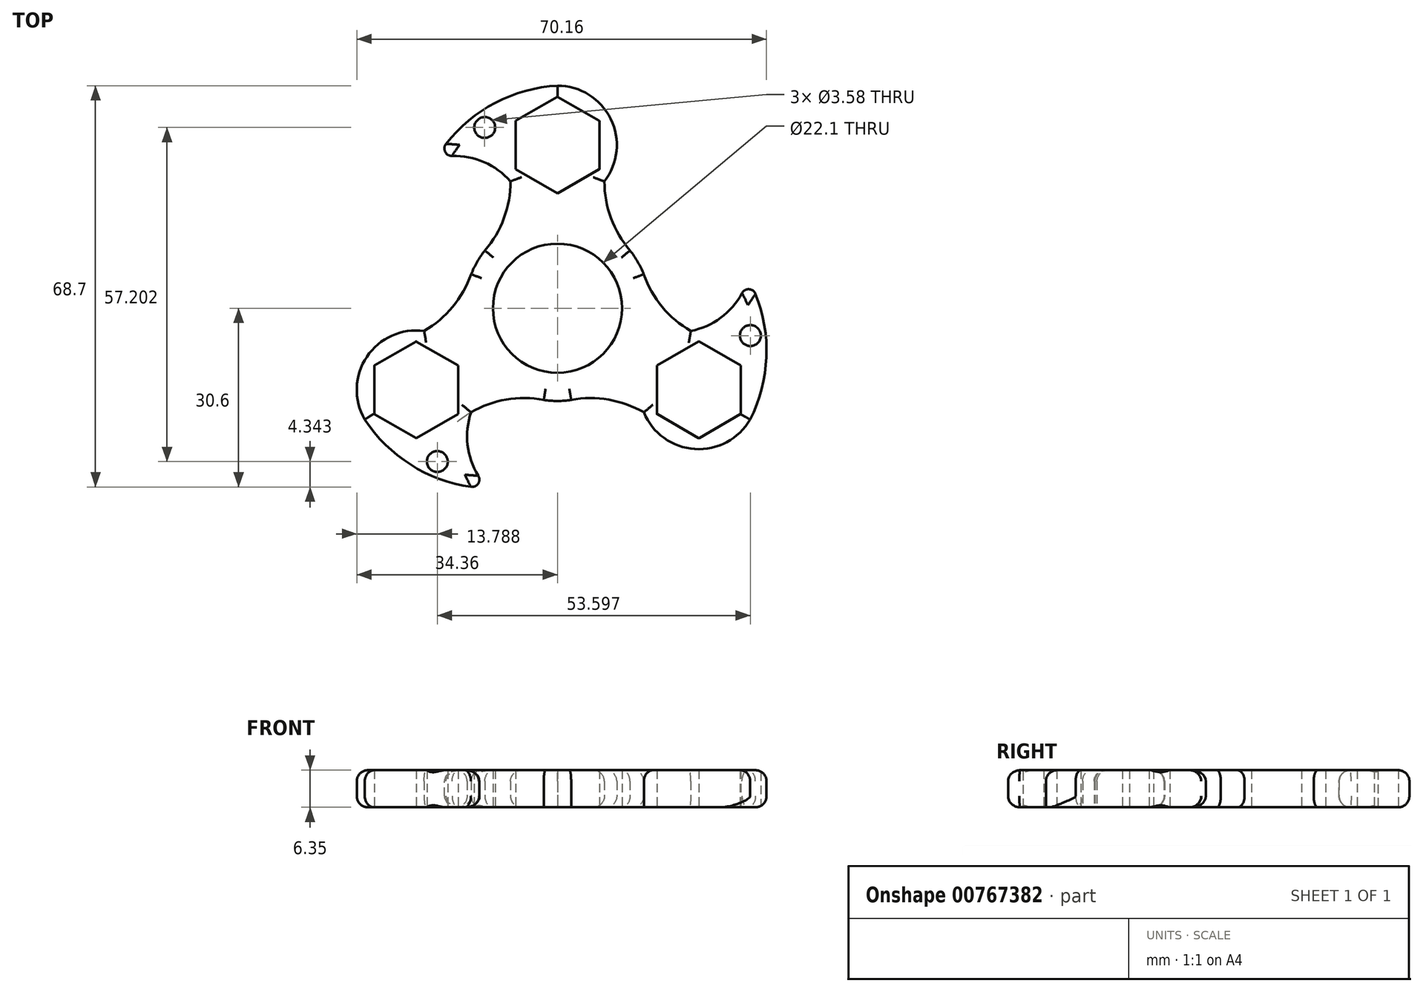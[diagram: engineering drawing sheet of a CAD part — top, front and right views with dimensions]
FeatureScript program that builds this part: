
annotation { "Feature Type Name" : "Feature", "Feature Type Description" : "" }
export const myFeature = defineFeature(function(context is Context, id is Id, definition is map)
    precondition{}
    {
        {
            var Q0;
            Q0=qCreatedBy(makeId("Top.planeOp"),FACE);
            var sketch = newSketch(context, id + "F0", { "sketchPlane" : qUnion([Q0])});
            skCircle(sketch, "E0", {"center": v(0, 0) * mm, "radius": 38.1 * mm});
            skCircle(sketch, "E1", {"center": v(0, 0) * mm, "radius": 11.05 * mm});
            skCircle(sketch, "E2.cCircle", {"center": v(0, 27.94) * mm, "radius": 8.29 * mm, "construction": true});
            skLineSegment(sketch, "E2.0", {"start": v(0, 36.23) * mm, "end": v(7.18, 32.08) * mm});
            skLineSegment(sketch, "E2.1", {"start": v(7.18, 32.08) * mm, "end": v(7.18, 23.8) * mm});
            skLineSegment(sketch, "E2.2", {"start": v(7.18, 23.8) * mm, "end": v(0, 19.65) * mm});
            skLineSegment(sketch, "E2.3", {"start": v(0, 19.65) * mm, "end": v(-7.18, 23.8) * mm});
            skLineSegment(sketch, "E2.4", {"start": v(-7.18, 23.8) * mm, "end": v(-7.18, 32.08) * mm});
            skLineSegment(sketch, "E2.5", {"start": v(-7.18, 32.08) * mm, "end": v(0, 36.23) * mm});
            skCircle(sketch, "E3", {"center": v(0, 27.94) * mm, "radius": 10.16 * mm});
            skCircle(sketch, "E4", {"center": v(0, 0) * mm, "radius": 15.88 * mm});
            skArc(sketch, "E5", {"start": v(8.04, 21.73) * mm, "mid": v(9.17, 15.41) * mm, "end": v(12.42, 9.88) * mm});
            skPoint(sketch, "E5.startSnap0", {"position": v(-3.59, 21.73) * mm});
            skArc(sketch, "E6", {"start": v(-12.42, 9.88) * mm, "mid": v(-9.16, 15.4) * mm, "end": v(-8.04, 21.73) * mm});
            skArc(sketch, "E7", {"start": v(0, 38.1) * mm, "mid": v(-11.9, 34.46) * mm, "end": v(-20.76, 25.7) * mm});
            skArc(sketch, "E8", {"start": v(-8.04, 21.73) * mm, "mid": v(-13.84, 25.5) * mm, "end": v(-20.76, 25.7) * mm});
            skCircle(sketch, "E9", {"center": v(-12.45, 30.94) * mm, "radius": 1.79 * mm});
            skArc(sketch, "E10.1.0", {"start": v(-14.8, -17.82) * mm, "mid": v(-15.16, -24.73) * mm, "end": v(-11.88, -30.83) * mm});
            skArc(sketch, "E10.1.1", {"start": v(-2.35, -15.7) * mm, "mid": v(-8.76, -15.64) * mm, "end": v(-14.8, -17.82) * mm});
            skArc(sketch, "E10.1.2", {"start": v(-33, -19.05) * mm, "mid": v(-23.89, -27.54) * mm, "end": v(-11.88, -30.83) * mm});
            skCircle(sketch, "E10.1.3", {"center": v(-24.2, -13.97) * mm, "radius": 10.16 * mm});
            skArc(sketch, "E10.1.4", {"start": v(-22.83, -3.9) * mm, "mid": v(-17.94, 0.24) * mm, "end": v(-14.77, 5.82) * mm});
            skCircle(sketch, "E10.1.5", {"center": v(-20.57, -26.26) * mm, "radius": 1.79 * mm});
            skLineSegment(sketch, "E10.1.6", {"start": v(-17.02, -18.11) * mm, "end": v(-24.2, -22.26) * mm});
            skLineSegment(sketch, "E10.1.7", {"start": v(-24.2, -22.26) * mm, "end": v(-31.37, -18.11) * mm});
            skLineSegment(sketch, "E10.1.8", {"start": v(-31.37, -18.11) * mm, "end": v(-31.37, -9.83) * mm});
            skLineSegment(sketch, "E10.1.9", {"start": v(-31.37, -9.83) * mm, "end": v(-24.2, -5.68) * mm});
            skLineSegment(sketch, "E10.1.10", {"start": v(-24.2, -5.68) * mm, "end": v(-17.02, -9.83) * mm});
            skLineSegment(sketch, "E10.1.11", {"start": v(-17.02, -9.83) * mm, "end": v(-17.02, -18.11) * mm});
            skArc(sketch, "E10.2.0", {"start": v(22.83, -3.9) * mm, "mid": v(29, -0.76) * mm, "end": v(32.64, 5.13) * mm});
            skArc(sketch, "E10.2.1", {"start": v(14.77, 5.82) * mm, "mid": v(17.93, 0.23) * mm, "end": v(22.83, -3.9) * mm});
            skArc(sketch, "E10.2.2", {"start": v(33, -19.05) * mm, "mid": v(35.8, -6.92) * mm, "end": v(32.64, 5.13) * mm});
            skCircle(sketch, "E10.2.3", {"center": v(24.2, -13.97) * mm, "radius": 10.16 * mm});
            skArc(sketch, "E10.2.4", {"start": v(14.8, -17.82) * mm, "mid": v(8.76, -15.65) * mm, "end": v(2.35, -15.7) * mm});
            skCircle(sketch, "E10.2.5", {"center": v(33.03, -4.69) * mm, "radius": 1.79 * mm});
            skLineSegment(sketch, "E10.2.6", {"start": v(24.2, -5.68) * mm, "end": v(31.37, -9.83) * mm});
            skLineSegment(sketch, "E10.2.7", {"start": v(31.37, -9.83) * mm, "end": v(31.37, -18.11) * mm});
            skLineSegment(sketch, "E10.2.8", {"start": v(31.37, -18.11) * mm, "end": v(24.2, -22.26) * mm});
            skLineSegment(sketch, "E10.2.9", {"start": v(24.2, -22.26) * mm, "end": v(17.02, -18.11) * mm});
            skLineSegment(sketch, "E10.2.10", {"start": v(17.02, -18.11) * mm, "end": v(17.02, -9.83) * mm});
            skLineSegment(sketch, "E10.2.11", {"start": v(17.02, -9.83) * mm, "end": v(24.2, -5.68) * mm});
            skSolve(sketch);
        }
        {
            var Q0;
            {var subQ0=sQuery(id+"F0.wireOp",EDGE,"E5");Q0=makeQuery(id+"F0.imprint","IMPRINT",FACE,{"disambiguationData":[TD([[makeQuery(id+"F0.imprint","IMPRINT",EDGE,{"derivedFrom":subQ0}),-1.0]])]});}
            var Q1;
            Q1=makeQuery(id+"F0.imprint","IMPRINT",FACE,{"disambiguationData":[TD([[makeQuery(id+"F0.imprint","IMPRINT",EDGE,{"derivedFrom":sQuery(id+"F0.wireOp",EDGE,"E2.0")}),1.0]])]});
            var Q2;
            {var subQ0=sQuery(id+"F0.wireOp",EDGE,"E8");Q2=makeQuery(id+"F0.imprint","IMPRINT",FACE,{"disambiguationData":[TD([[makeQuery(id+"F0.imprint","IMPRINT",EDGE,{"derivedFrom":subQ0}),-1.0]])]});}
            var Q3;
            Q3=makeQuery(id+"F0.imprint","IMPRINT",FACE,{"disambiguationData":[TD([[makeQuery(id+"F0.imprint","IMPRINT",EDGE,{"derivedFrom":sQuery(id+"F0.wireOp",EDGE,"E1")}),-1.0]])]});
            var Q4;
            Q4=makeQuery(id+"F0.imprint","IMPRINT",FACE,{"disambiguationData":[TD([[makeQuery(id+"F0.imprint","IMPRINT",EDGE,{"derivedFrom":sQuery(id+"F0.wireOp",EDGE,"E10.1.6")}),1.0]])]});
            var Q5;
            {var subQ0=sQuery(id+"F0.wireOp",EDGE,"E10.1.1");Q5=makeQuery(id+"F0.imprint","IMPRINT",FACE,{"disambiguationData":[TD([[makeQuery(id+"F0.imprint","IMPRINT",EDGE,{"derivedFrom":subQ0}),-1.0]])]});}
            var Q6;
            {var subQ1=sQuery(id+"F0.wireOp",EDGE,"E10.1.0");Q6=makeQuery(id+"F0.imprint","IMPRINT",FACE,{"disambiguationData":[TD([[makeQuery(id+"F0.imprint","IMPRINT",EDGE,{"derivedFrom":subQ1}),-1.0]])]});}
            var Q7;
            {var subQ0=sQuery(id+"F0.wireOp",EDGE,"E10.2.1");Q7=makeQuery(id+"F0.imprint","IMPRINT",FACE,{"disambiguationData":[TD([[makeQuery(id+"F0.imprint","IMPRINT",EDGE,{"derivedFrom":subQ0}),-1.0]])]});}
            var Q8;
            Q8=makeQuery(id+"F0.imprint","IMPRINT",FACE,{"disambiguationData":[TD([[makeQuery(id+"F0.imprint","IMPRINT",EDGE,{"derivedFrom":sQuery(id+"F0.wireOp",EDGE,"E10.2.6")}),1.0]])]});
            var Q9;
            {var subQ1=sQuery(id+"F0.wireOp",EDGE,"E10.2.0");Q9=makeQuery(id+"F0.imprint","IMPRINT",FACE,{"disambiguationData":[TD([[makeQuery(id+"F0.imprint","IMPRINT",EDGE,{"derivedFrom":subQ1}),-1.0]])]});}
            extrude(context, id + "F1", {"entities" : qUnion([Q0, Q1, Q2, Q3, Q4, Q5, Q6, Q7, Q8, Q9]), "depth" : 6.35 * mm, "offsetDistance" : 25.4 * mm});
        }
        {
            var Q0;
            Q0=makeQuery(id+"F1.opExtrude","SWEPT_EDGE",EDGE,{"disambiguationData":[OSD([sQuery(id+"F0.wireOp",EDGE,"E7"),sQuery(id+"F0.wireOp",EDGE,"E8")])]});
            var Q1;
            Q1=makeQuery(id+"F1.opExtrude","SWEPT_EDGE",EDGE,{"disambiguationData":[OSD([sQuery(id+"F0.wireOp",EDGE,"E10.1.0"),sQuery(id+"F0.wireOp",EDGE,"E10.1.2")])]});
            var Q2;
            Q2=makeQuery(id+"F1.opExtrude","SWEPT_EDGE",EDGE,{"disambiguationData":[OSD([sQuery(id+"F0.wireOp",EDGE,"E10.2.0"),sQuery(id+"F0.wireOp",EDGE,"E10.2.2")])]});
            fillet(context, id + "F2", {"entities" : qUnion([Q0, Q1, Q2]), "radius" : 1.27 * mm, "tangentPropagation" : true, "allowEdgeOverflow" : false});
        }
        {
            var Q0;
            {var subQ0=sQuery(id+"F0.wireOp",EDGE,"E10.1.2");var subQ1=sQuery(id+"F0.wireOp",EDGE,"E10.1.0");Q0=makeQuery(id+"F2.opFillet","BLEND_EDGE",EDGE,{"blendedFrom":[makeQuery(id+"F1.opExtrude","SWEPT_EDGE",EDGE,{"disambiguationData":[OSD([subQ1,subQ0])]}),makeQuery(id+"F1.opExtrude","CAP_FACE",FACE,{"disambiguationData":[OSD([sQuery(id+"F0.wireOp",EDGE,"E1"),sQuery(id+"F0.wireOp",EDGE,"E2.0"),sQuery(id+"F0.wireOp",EDGE,"E2.1"),sQuery(id+"F0.wireOp",EDGE,"E2.2"),sQuery(id+"F0.wireOp",EDGE,"E2.3"),sQuery(id+"F0.wireOp",EDGE,"E2.4"),sQuery(id+"F0.wireOp",EDGE,"E2.5"),sQuery(id+"F0.wireOp",EDGE,"E3"),sQuery(id+"F0.wireOp",EDGE,"E4"),sQuery(id+"F0.wireOp",EDGE,"E5"),sQuery(id+"F0.wireOp",EDGE,"E6"),sQuery(id+"F0.wireOp",EDGE,"E7"),sQuery(id+"F0.wireOp",EDGE,"E8"),sQuery(id+"F0.wireOp",EDGE,"E9"),subQ1,sQuery(id+"F0.wireOp",EDGE,"E10.1.1"),subQ0,sQuery(id+"F0.wireOp",EDGE,"E10.1.3"),sQuery(id+"F0.wireOp",EDGE,"E10.1.4"),sQuery(id+"F0.wireOp",EDGE,"E10.1.5"),sQuery(id+"F0.wireOp",EDGE,"E10.1.6"),sQuery(id+"F0.wireOp",EDGE,"E10.1.7"),sQuery(id+"F0.wireOp",EDGE,"E10.1.8"),sQuery(id+"F0.wireOp",EDGE,"E10.1.9"),sQuery(id+"F0.wireOp",EDGE,"E10.1.10"),sQuery(id+"F0.wireOp",EDGE,"E10.1.11"),sQuery(id+"F0.wireOp",EDGE,"E10.2.0"),sQuery(id+"F0.wireOp",EDGE,"E10.2.1"),sQuery(id+"F0.wireOp",EDGE,"E10.2.2"),sQuery(id+"F0.wireOp",EDGE,"E10.2.3"),sQuery(id+"F0.wireOp",EDGE,"E10.2.4"),sQuery(id+"F0.wireOp",EDGE,"E10.2.5"),sQuery(id+"F0.wireOp",EDGE,"E10.2.6"),sQuery(id+"F0.wireOp",EDGE,"E10.2.7"),sQuery(id+"F0.wireOp",EDGE,"E10.2.8"),sQuery(id+"F0.wireOp",EDGE,"E10.2.9"),sQuery(id+"F0.wireOp",EDGE,"E10.2.10"),sQuery(id+"F0.wireOp",EDGE,"E10.2.11")])],"isStart":false})],"blendedInto":[makeQuery(id+"F1.opExtrude","CAP_FACE",FACE,{"disambiguationData":[OSD([sQuery(id+"F0.wireOp",EDGE,"E1"),sQuery(id+"F0.wireOp",EDGE,"E2.0"),sQuery(id+"F0.wireOp",EDGE,"E2.1"),sQuery(id+"F0.wireOp",EDGE,"E2.2"),sQuery(id+"F0.wireOp",EDGE,"E2.3"),sQuery(id+"F0.wireOp",EDGE,"E2.4"),sQuery(id+"F0.wireOp",EDGE,"E2.5"),sQuery(id+"F0.wireOp",EDGE,"E3"),sQuery(id+"F0.wireOp",EDGE,"E4"),sQuery(id+"F0.wireOp",EDGE,"E5"),sQuery(id+"F0.wireOp",EDGE,"E6"),sQuery(id+"F0.wireOp",EDGE,"E7"),sQuery(id+"F0.wireOp",EDGE,"E8"),sQuery(id+"F0.wireOp",EDGE,"E9"),subQ1,sQuery(id+"F0.wireOp",EDGE,"E10.1.1"),subQ0,sQuery(id+"F0.wireOp",EDGE,"E10.1.3"),sQuery(id+"F0.wireOp",EDGE,"E10.1.4"),sQuery(id+"F0.wireOp",EDGE,"E10.1.5"),sQuery(id+"F0.wireOp",EDGE,"E10.1.6"),sQuery(id+"F0.wireOp",EDGE,"E10.1.7"),sQuery(id+"F0.wireOp",EDGE,"E10.1.8"),sQuery(id+"F0.wireOp",EDGE,"E10.1.9"),sQuery(id+"F0.wireOp",EDGE,"E10.1.10"),sQuery(id+"F0.wireOp",EDGE,"E10.1.11"),sQuery(id+"F0.wireOp",EDGE,"E10.2.0"),sQuery(id+"F0.wireOp",EDGE,"E10.2.1"),sQuery(id+"F0.wireOp",EDGE,"E10.2.2"),sQuery(id+"F0.wireOp",EDGE,"E10.2.3"),sQuery(id+"F0.wireOp",EDGE,"E10.2.4"),sQuery(id+"F0.wireOp",EDGE,"E10.2.5"),sQuery(id+"F0.wireOp",EDGE,"E10.2.6"),sQuery(id+"F0.wireOp",EDGE,"E10.2.7"),sQuery(id+"F0.wireOp",EDGE,"E10.2.8"),sQuery(id+"F0.wireOp",EDGE,"E10.2.9"),sQuery(id+"F0.wireOp",EDGE,"E10.2.10"),sQuery(id+"F0.wireOp",EDGE,"E10.2.11")])],"isStart":false})]});}
            var Q1;
            Q1=makeQuery(id+"F1.opExtrude","CAP_EDGE",EDGE,{"disambiguationData":[OSD([sQuery(id+"F0.wireOp",EDGE,"E10.1.1")])],"isStart":false});
            var Q2;
            Q2=makeQuery(id+"F1.opExtrude","CAP_EDGE",EDGE,{"disambiguationData":[OSD([sQuery(id+"F0.wireOp",EDGE,"E10.1.0")])],"isStart":false});
            var Q3;
            Q3=makeQuery(id+"F1.opExtrude","CAP_EDGE",EDGE,{"disambiguationData":[OSD([sQuery(id+"F0.wireOp",EDGE,"E10.2.4")])],"isStart":false});
            var Q4;
            Q4=makeQuery(id+"F1.opExtrude","CAP_EDGE",EDGE,{"disambiguationData":[OSD([sQuery(id+"F0.wireOp",EDGE,"E10.2.3")])],"isStart":false});
            var Q5;
            Q5=makeQuery(id+"F1.opExtrude","CAP_EDGE",EDGE,{"disambiguationData":[OSD([sQuery(id+"F0.wireOp",EDGE,"E10.2.2")])],"isStart":false});
            var Q6;
            Q6=makeQuery(id+"F1.opExtrude","CAP_EDGE",EDGE,{"disambiguationData":[OSD([sQuery(id+"F0.wireOp",EDGE,"E10.2.1")])],"isStart":false});
            var Q7;
            Q7=makeQuery(id+"F1.opExtrude","CAP_EDGE",EDGE,{"disambiguationData":[OSD([sQuery(id+"F0.wireOp",EDGE,"E5")])],"isStart":false});
            var Q8;
            Q8=makeQuery(id+"F1.opExtrude","CAP_EDGE",EDGE,{"disambiguationData":[OSD([sQuery(id+"F0.wireOp",EDGE,"E3")])],"isStart":false});
            var Q9;
            Q9=makeQuery(id+"F1.opExtrude","CAP_EDGE",EDGE,{"disambiguationData":[OSD([sQuery(id+"F0.wireOp",EDGE,"E7")])],"isStart":false});
            var Q10;
            Q10=makeQuery(id+"F1.opExtrude","CAP_EDGE",EDGE,{"disambiguationData":[OSD([sQuery(id+"F0.wireOp",EDGE,"E6")])],"isStart":false});
            var Q11;
            Q11=makeQuery(id+"F1.opExtrude","CAP_EDGE",EDGE,{"disambiguationData":[OSD([sQuery(id+"F0.wireOp",EDGE,"E10.1.4")])],"isStart":false});
            var Q12;
            Q12=makeQuery(id+"F1.opExtrude","CAP_EDGE",EDGE,{"disambiguationData":[OSD([sQuery(id+"F0.wireOp",EDGE,"E10.1.3")])],"isStart":false});
            var Q13;
            Q13=makeQuery(id+"F1.opExtrude","CAP_EDGE",EDGE,{"disambiguationData":[OSD([sQuery(id+"F0.wireOp",EDGE,"E10.1.4")])],"isStart":true});
            var Q14;
            Q14=makeQuery(id+"F1.opExtrude","CAP_EDGE",EDGE,{"disambiguationData":[OSD([sQuery(id+"F0.wireOp",EDGE,"E6")])],"isStart":true});
            var Q15;
            Q15=makeQuery(id+"F1.opExtrude","CAP_EDGE",EDGE,{"disambiguationData":[OSD([sQuery(id+"F0.wireOp",EDGE,"E10.1.3")])],"isStart":true});
            var Q16;
            Q16=makeQuery(id+"F1.opExtrude","CAP_EDGE",EDGE,{"disambiguationData":[OSD([sQuery(id+"F0.wireOp",EDGE,"E10.1.2")])],"isStart":true});
            var Q17;
            Q17=makeQuery(id+"F1.opExtrude","CAP_EDGE",EDGE,{"disambiguationData":[OSD([sQuery(id+"F0.wireOp",EDGE,"E7")])],"isStart":true});
            var Q18;
            {var subQ0=sQuery(id+"F0.wireOp",EDGE,"E8");var subQ1=sQuery(id+"F0.wireOp",EDGE,"E7");Q18=makeQuery(id+"F2.opFillet","BLEND_EDGE",EDGE,{"blendedFrom":[makeQuery(id+"F1.opExtrude","SWEPT_EDGE",EDGE,{"disambiguationData":[OSD([subQ1,subQ0])]}),makeQuery(id+"F1.opExtrude","CAP_FACE",FACE,{"disambiguationData":[OSD([sQuery(id+"F0.wireOp",EDGE,"E1"),sQuery(id+"F0.wireOp",EDGE,"E2.0"),sQuery(id+"F0.wireOp",EDGE,"E2.1"),sQuery(id+"F0.wireOp",EDGE,"E2.2"),sQuery(id+"F0.wireOp",EDGE,"E2.3"),sQuery(id+"F0.wireOp",EDGE,"E2.4"),sQuery(id+"F0.wireOp",EDGE,"E2.5"),sQuery(id+"F0.wireOp",EDGE,"E3"),sQuery(id+"F0.wireOp",EDGE,"E4"),sQuery(id+"F0.wireOp",EDGE,"E5"),sQuery(id+"F0.wireOp",EDGE,"E6"),subQ1,subQ0,sQuery(id+"F0.wireOp",EDGE,"E9"),sQuery(id+"F0.wireOp",EDGE,"E10.1.0"),sQuery(id+"F0.wireOp",EDGE,"E10.1.1"),sQuery(id+"F0.wireOp",EDGE,"E10.1.2"),sQuery(id+"F0.wireOp",EDGE,"E10.1.3"),sQuery(id+"F0.wireOp",EDGE,"E10.1.4"),sQuery(id+"F0.wireOp",EDGE,"E10.1.5"),sQuery(id+"F0.wireOp",EDGE,"E10.1.6"),sQuery(id+"F0.wireOp",EDGE,"E10.1.7"),sQuery(id+"F0.wireOp",EDGE,"E10.1.8"),sQuery(id+"F0.wireOp",EDGE,"E10.1.9"),sQuery(id+"F0.wireOp",EDGE,"E10.1.10"),sQuery(id+"F0.wireOp",EDGE,"E10.1.11"),sQuery(id+"F0.wireOp",EDGE,"E10.2.0"),sQuery(id+"F0.wireOp",EDGE,"E10.2.1"),sQuery(id+"F0.wireOp",EDGE,"E10.2.2"),sQuery(id+"F0.wireOp",EDGE,"E10.2.3"),sQuery(id+"F0.wireOp",EDGE,"E10.2.4"),sQuery(id+"F0.wireOp",EDGE,"E10.2.5"),sQuery(id+"F0.wireOp",EDGE,"E10.2.6"),sQuery(id+"F0.wireOp",EDGE,"E10.2.7"),sQuery(id+"F0.wireOp",EDGE,"E10.2.8"),sQuery(id+"F0.wireOp",EDGE,"E10.2.9"),sQuery(id+"F0.wireOp",EDGE,"E10.2.10"),sQuery(id+"F0.wireOp",EDGE,"E10.2.11")])],"isStart":true})],"blendedInto":[makeQuery(id+"F1.opExtrude","CAP_FACE",FACE,{"disambiguationData":[OSD([sQuery(id+"F0.wireOp",EDGE,"E1"),sQuery(id+"F0.wireOp",EDGE,"E2.0"),sQuery(id+"F0.wireOp",EDGE,"E2.1"),sQuery(id+"F0.wireOp",EDGE,"E2.2"),sQuery(id+"F0.wireOp",EDGE,"E2.3"),sQuery(id+"F0.wireOp",EDGE,"E2.4"),sQuery(id+"F0.wireOp",EDGE,"E2.5"),sQuery(id+"F0.wireOp",EDGE,"E3"),sQuery(id+"F0.wireOp",EDGE,"E4"),sQuery(id+"F0.wireOp",EDGE,"E5"),sQuery(id+"F0.wireOp",EDGE,"E6"),subQ1,subQ0,sQuery(id+"F0.wireOp",EDGE,"E9"),sQuery(id+"F0.wireOp",EDGE,"E10.1.0"),sQuery(id+"F0.wireOp",EDGE,"E10.1.1"),sQuery(id+"F0.wireOp",EDGE,"E10.1.2"),sQuery(id+"F0.wireOp",EDGE,"E10.1.3"),sQuery(id+"F0.wireOp",EDGE,"E10.1.4"),sQuery(id+"F0.wireOp",EDGE,"E10.1.5"),sQuery(id+"F0.wireOp",EDGE,"E10.1.6"),sQuery(id+"F0.wireOp",EDGE,"E10.1.7"),sQuery(id+"F0.wireOp",EDGE,"E10.1.8"),sQuery(id+"F0.wireOp",EDGE,"E10.1.9"),sQuery(id+"F0.wireOp",EDGE,"E10.1.10"),sQuery(id+"F0.wireOp",EDGE,"E10.1.11"),sQuery(id+"F0.wireOp",EDGE,"E10.2.0"),sQuery(id+"F0.wireOp",EDGE,"E10.2.1"),sQuery(id+"F0.wireOp",EDGE,"E10.2.2"),sQuery(id+"F0.wireOp",EDGE,"E10.2.3"),sQuery(id+"F0.wireOp",EDGE,"E10.2.4"),sQuery(id+"F0.wireOp",EDGE,"E10.2.5"),sQuery(id+"F0.wireOp",EDGE,"E10.2.6"),sQuery(id+"F0.wireOp",EDGE,"E10.2.7"),sQuery(id+"F0.wireOp",EDGE,"E10.2.8"),sQuery(id+"F0.wireOp",EDGE,"E10.2.9"),sQuery(id+"F0.wireOp",EDGE,"E10.2.10"),sQuery(id+"F0.wireOp",EDGE,"E10.2.11")])],"isStart":true})]});}
            var Q19;
            Q19=makeQuery(id+"F1.opExtrude","CAP_EDGE",EDGE,{"disambiguationData":[OSD([sQuery(id+"F0.wireOp",EDGE,"E3")])],"isStart":true});
            var Q20;
            Q20=makeQuery(id+"F1.opExtrude","CAP_EDGE",EDGE,{"disambiguationData":[OSD([sQuery(id+"F0.wireOp",EDGE,"E5")])],"isStart":true});
            var Q21;
            Q21=makeQuery(id+"F1.opExtrude","CAP_EDGE",EDGE,{"disambiguationData":[OSD([sQuery(id+"F0.wireOp",EDGE,"E10.2.1")])],"isStart":true});
            var Q22;
            Q22=makeQuery(id+"F1.opExtrude","CAP_EDGE",EDGE,{"disambiguationData":[OSD([sQuery(id+"F0.wireOp",EDGE,"E10.2.0")])],"isStart":true});
            fillet(context, id + "F3", {"entities" : qUnion([Q0, Q1, Q2, Q3, Q4, Q5, Q6, Q7, Q8, Q9, Q10, Q11, Q12, Q13, Q14, Q15, Q16, Q17, Q18, Q19, Q20, Q21, Q22]), "radius" : 1.9 * mm, "tangentPropagation" : true, "allowEdgeOverflow" : false});
        }
    });
